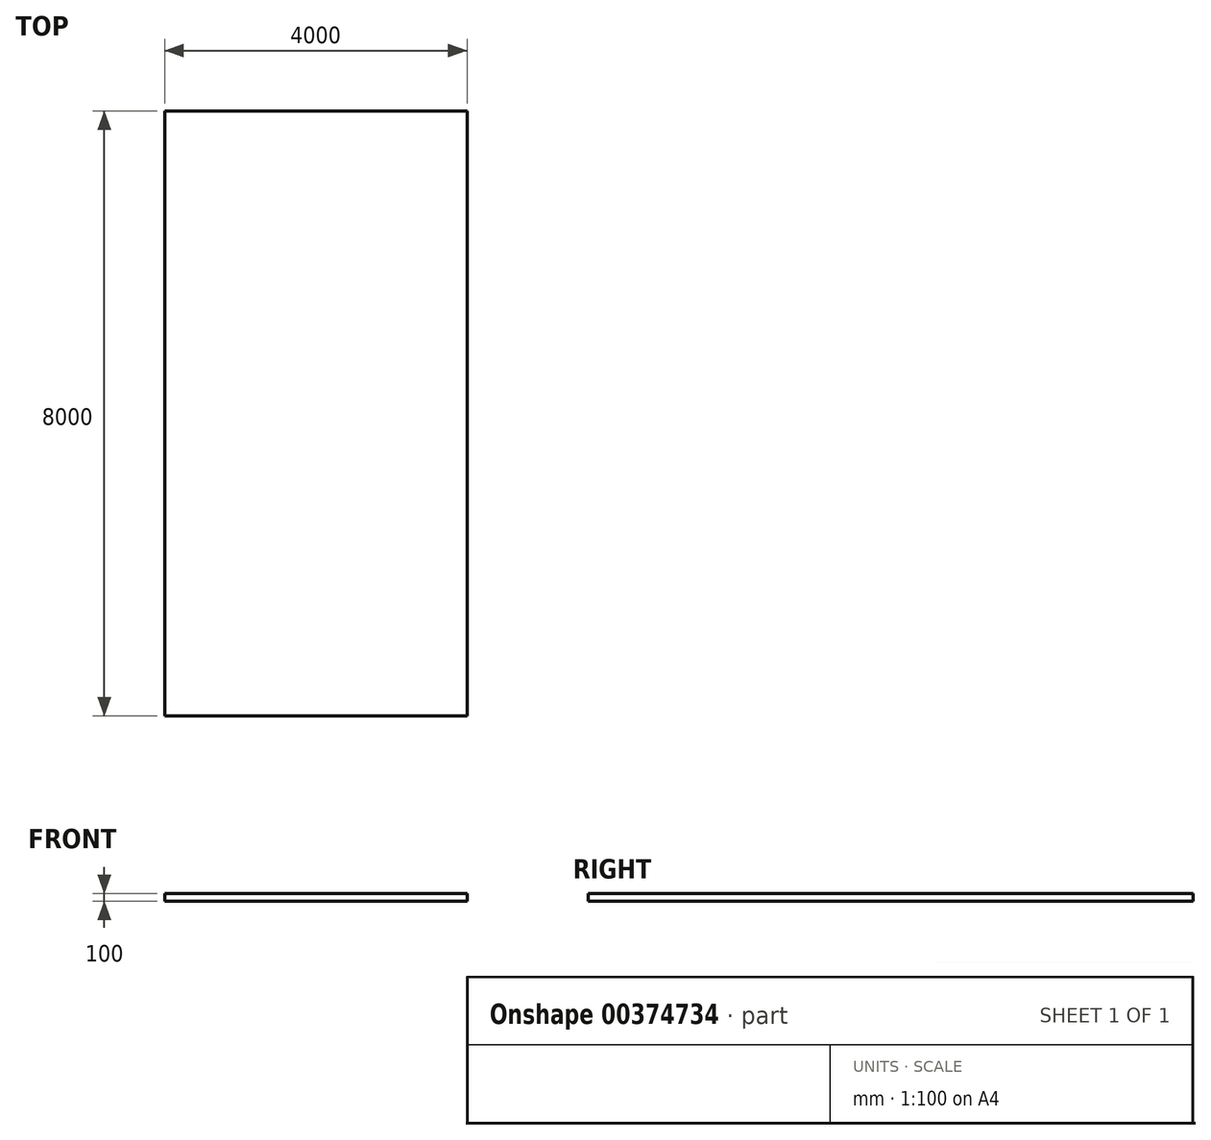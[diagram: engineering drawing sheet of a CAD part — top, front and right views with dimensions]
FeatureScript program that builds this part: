
annotation { "Feature Type Name" : "Feature", "Feature Type Description" : "" }
export const myFeature = defineFeature(function(context is Context, id is Id, definition is map)
    precondition{}
    {
        {
            var Q0;
            Q0=qCreatedBy(makeId("Top.planeOp"),FACE);
            var sketch = newSketch(context, id + "F0", { "sketchPlane" : qUnion([Q0])});
            skLineSegment(sketch, "E0.bottom", {"start": v(0, 0) * mm, "end": v(4000, 0) * mm});
            skLineSegment(sketch, "E0.top", {"start": v(0, 8000) * mm, "end": v(4000, 8000) * mm});
            skLineSegment(sketch, "E0.left", {"start": v(0, 0) * mm, "end": v(0, 8000) * mm});
            skLineSegment(sketch, "E0.right", {"start": v(4000, 0) * mm, "end": v(4000, 8000) * mm});
            skLineSegment(sketch, "E1.bottom", {"start": v(-100, -100) * mm, "end": v(4100, -100) * mm});
            skLineSegment(sketch, "E1.top", {"start": v(-100, 8100) * mm, "end": v(4100, 8100) * mm});
            skLineSegment(sketch, "E1.left", {"start": v(-100, -100) * mm, "end": v(-100, 8100) * mm});
            skLineSegment(sketch, "E1.right", {"start": v(4100, -100) * mm, "end": v(4100, 8100) * mm});
            skSolve(sketch);
        }
        {
            var Q0;
            Q0=makeQuery(id+"F0.imprint","IMPRINT",FACE,{"disambiguationData":[TD([[makeQuery(id+"F0.imprint","IMPRINT",EDGE,{"derivedFrom":sQuery(id+"F0.wireOp",EDGE,"E0.bottom")}),1.0]])]});
            extrude(context, id + "F1", {"entities" : qUnion([Q0]), "oppositeDirection" : true, "depth" : 100 * mm});
        }
    });
